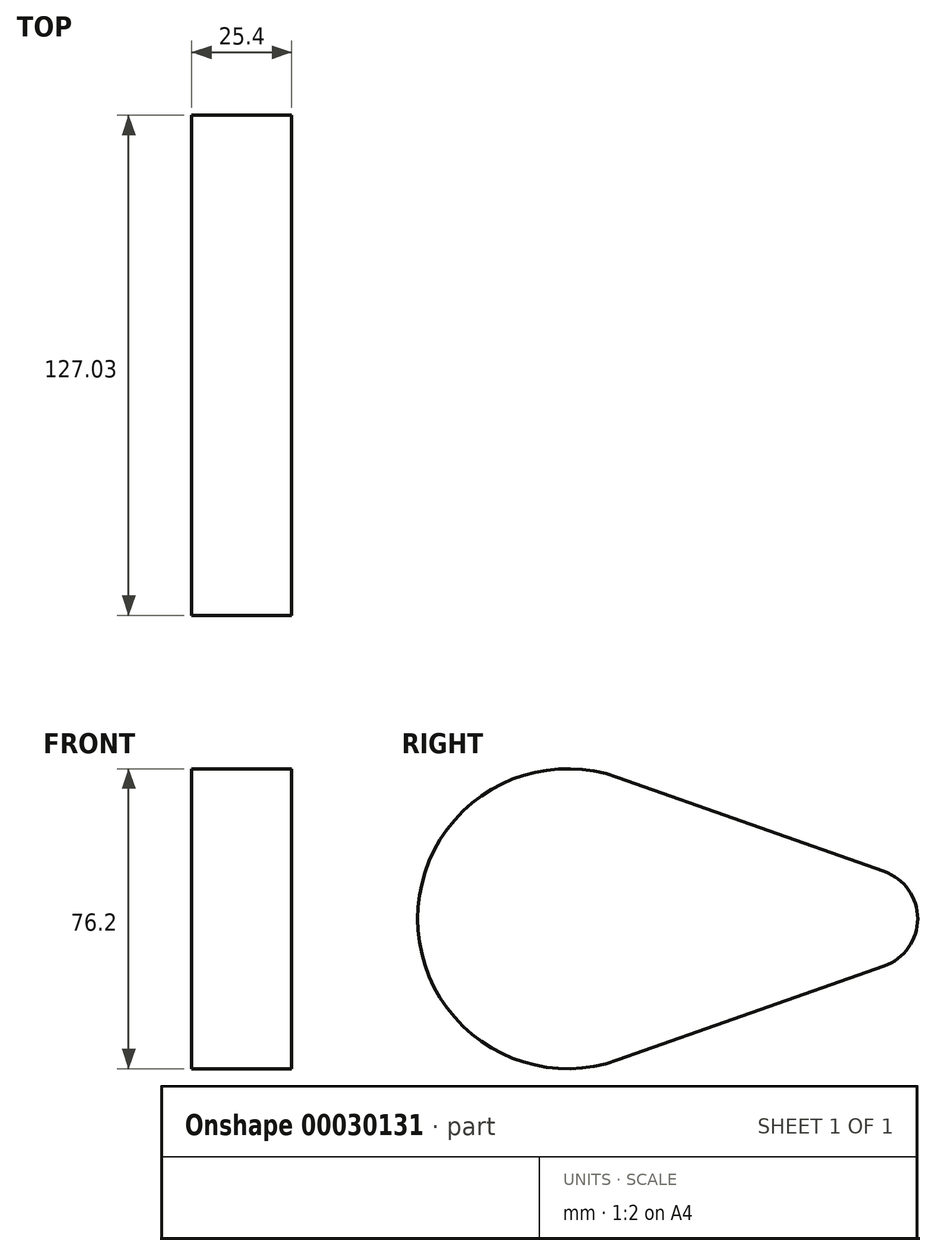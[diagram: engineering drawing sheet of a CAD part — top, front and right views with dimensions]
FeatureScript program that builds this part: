
annotation { "Feature Type Name" : "Feature", "Feature Type Description" : "" }
export const myFeature = defineFeature(function(context is Context, id is Id, definition is map)
    precondition{}
    {
        {
            var Q0;
            Q0=qCreatedBy(makeId("Right.planeOp"),FACE);
            var sketch = newSketch(context, id + "F0", { "sketchPlane" : qUnion([Q0])});
            skCircle(sketch, "E0", {"center": v(0, 0) * mm, "radius": 38.1 * mm});
            skCircle(sketch, "E1", {"center": v(76.23, 0) * mm, "radius": 12.7 * mm});
            skLineSegment(sketch, "E2", {"start": v(12.7, 35.92) * mm, "end": v(80.46, 11.97) * mm});
            skLineSegment(sketch, "E3", {"start": v(12.7, -35.92) * mm, "end": v(80.46, -11.97) * mm});
            skSolve(sketch);
        }
        {
            var Q0;
            {var subQ0=sQuery(id+"F0.wireOp",EDGE,"E1");var subQ2=makeQuery(id+"F0.imprint","INTERSECT",VERTEX,{"derivedFrom":[subQ0,sQuery(id+"F0.wireOp",EDGE,"E2")]});Q0=makeQuery(id+"F0.imprint","IMPRINT",FACE,{"disambiguationData":[TD([[makeQuery(id+"F0.imprint","IMPRINT",EDGE,{"disambiguationData":[TD([[subQ2,-1.0]])],"derivedFrom":subQ0}),1.0]])]});}
            var Q1;
            {var subQ1=sQuery(id+"F0.wireOp",EDGE,"E2");Q1=makeQuery(id+"F0.imprint","IMPRINT",FACE,{"disambiguationData":[TD([[makeQuery(id+"F0.imprint","IMPRINT",EDGE,{"derivedFrom":subQ1}),-1.0]])]});}
            var Q2;
            {var subQ0=sQuery(id+"F0.wireOp",EDGE,"E0");var subQ2=makeQuery(id+"F0.imprint","INTERSECT",VERTEX,{"derivedFrom":[subQ0,sQuery(id+"F0.wireOp",EDGE,"E2")]});Q2=makeQuery(id+"F0.imprint","IMPRINT",FACE,{"disambiguationData":[TD([[makeQuery(id+"F0.imprint","IMPRINT",EDGE,{"disambiguationData":[TD([[subQ2,-1.0]])],"derivedFrom":subQ0}),1.0]])]});}
            extrude(context, id + "F1", {"entities" : qUnion([Q0, Q1, Q2]), "depth" : 25.4 * mm});
        }
    });
